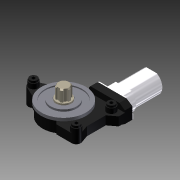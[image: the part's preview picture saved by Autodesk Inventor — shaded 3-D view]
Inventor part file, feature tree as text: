
AUTODESK INVENTOR PART (.ipt)
format: ipt  version: 2014 SP1 (Build 180222100, 222)  size: 517,120 bytes
history: native  units: mm
features: extrude x20, sketch x14, plane x4, chamfer x3, projected_geometry x3, pattern_circular x2, revolve x1, hole x1, other x1, fillet x1
ambient origin geometry x8: Origin, YZ Plane, XZ Plane, XY Plane, X Axis, Y Axis, Z Axis, Center Point
bodies: Solid1 (feature_tree)
feature tree (50):
  sketch  "Sketch1"  dims[d0=72.0mm d1=4.8mm d2=0.0mm]
  extrude  "Extrusion1"  Depth=4.8mm TaperAngle=0.0deg
  extrude  "Extrusion2"  Depth=60.0mm
  extrude  "Extrusion3"  Depth=1.9mm TaperAngle=0.0deg
  extrude  "Extrusion4"  Depth=23.8mm
  extrude  "Extrusion5"  Depth=3.0mm
  extrude  "Extrusion6"  Depth=8.0mm
  extrude  "Extrusion7"  Depth=19.9mm
  chamfer  "Chamfer1"  Distance=6.7mm
  pattern_circular  "Circular Pattern1"  Count=6 Angle=360.0deg
  sketch  "Sketch6"  dims[d14=18.0mm d15=0.0mm d16=8.0mm]
  extrude  "Extrusion8"  Depth=14.2mm
  plane  "Work Plane1"
  extrude  "Extrusion9"  Depth=56.76mm
  extrude  "Extrusion10"  Depth=37.0mm
  extrude  "Extrusion11"  Depth=25.0mm
  revolve  "Revolution1"  [1 undecoded]
  extrude  "Extrusion20"  Depth=4.5mm
  pattern_circular  "Circular Pattern2"  [2 undecoded]
  extrude  "Extrusion12"  Depth=15.0mm
  extrude  "Extrusion13"  Depth=4.5mm TaperAngle=0.0deg
  hole  "Hole2"  [1 undecoded]
  plane  "Work Plane4"
  extrude  "Extrusion19"  Depth=17.0mm TaperAngle=0.0deg
  other  "Work Axis1"
  extrude  "Extrusion14"  Depth=14.0mm TaperAngle=0.0deg
  chamfer  "Chamfer2"  Distance=19.5mm
  chamfer  "Chamfer3"  Distance=3.0mm
  fillet  "Fillet1"  Radius=3.0mm
  sketch  "Sketch13"  dims[d31=101.5mm d32=56.76mm]
  extrude  "Extrusion15"  Depth=4.5mm
  extrude  "Extrusion16"  Depth=3.0mm TaperAngle=0.0deg
  extrude  "Extrusion17"  [1 undecoded]
  extrude  "Extrusion18"  Depth=31.0mm
  sketch  "Sketch2"  dims[d3=60.0mm d4=42.0mm]
  sketch  "Sketch3"  dims[d5=25.8mm d6=1.9mm d7=0.0mm]
  sketch  "Sketch4"  dims[d8=1.2mm d9=0.0mm d10=23.8mm]
  sketch  "Sketch5"  dims[d11=3.0mm d12=0.0mm d13=16.4mm]
  sketch  "Sketch7"  dims[d17=6.7mm d18=0.0mm d19=19.9mm]
  sketch  "Sketch10"  dims[d20=4.0mm d21=6.7mm d22=0.0mm]
  projected_geometry  "Projected Loop4"
  sketch  "Sketch11"  dims[d23=1.75mm d24=2.0mm d25=45.0deg d26=60.0mm d27=360.0deg]
  projected_geometry  "Projected Loop5"
  projected_geometry  "Projected Loop6"
  plane  "Work Plane2"
  plane  "Work Plane3"
  sketch  "Sketch12"  dims[d29=68.0mm d30=14.2mm]
  sketch  "Sketch14"  dims[d33=16.3mm d34=37.0mm]
  sketch  "Sketch15"  dims[d35=135.0deg d36=25.0mm]
  sketch  "Sketch16"  dims[d37=10.0mm d38=63.0mm d39=30.5mm d40=13.2mm d41=15.0mm d42=18.6mm d43=0.0mm d44=6.0mm d45=17.0mm d46=0.0mm d47=14.0mm d48=0.0mm d49=19.5mm d50=3.0mm d51=0.0mm d52=3.0mm d53=0.0mm d61=11.9mm d62=3.0mm d63=0.0mm d64=5.0mm d65=6.0mm d66=4.0mm d67=2.0mm d68=90.0deg d69=8.0mm d70=20.594885mm d71=-17.0mm d73=31.0mm d74=12.0mm d75=0.0mm d76=40.0mm d78=6.0mm d79=9.0mm d80=45.0deg d81=6.0mm d82=9.0mm d83=45.0deg d84=6.5mm d85=34.9mm d86=19.95mm d88=3.75mm d89=17.45mm d90=3.0mm d91=10.0mm d92=2.0mm d93=0.0mm d94=15.0mm d95=0.0mm d96=60.0mm d97=0.0mm d98=67.0mm d99=0.0mm d100=0.2mm d101=3.55mm d102=-36.2mm d103=67.0mm d104=0.0mm d106=19.6mm d107=3.8mm d108=90.0deg d109=30.0deg d110=1.0mm d111=19.0mm d112=2.0mm d113=1.0mm d114=4.5mm d115=0.0mm d116=120.0mm d117=360.0deg]
note: 5 required parameter values undecoded (feature->parameter linkage not recoverable at this tier; creation-order binding heuristic only, values carry confidence <= 0.55)